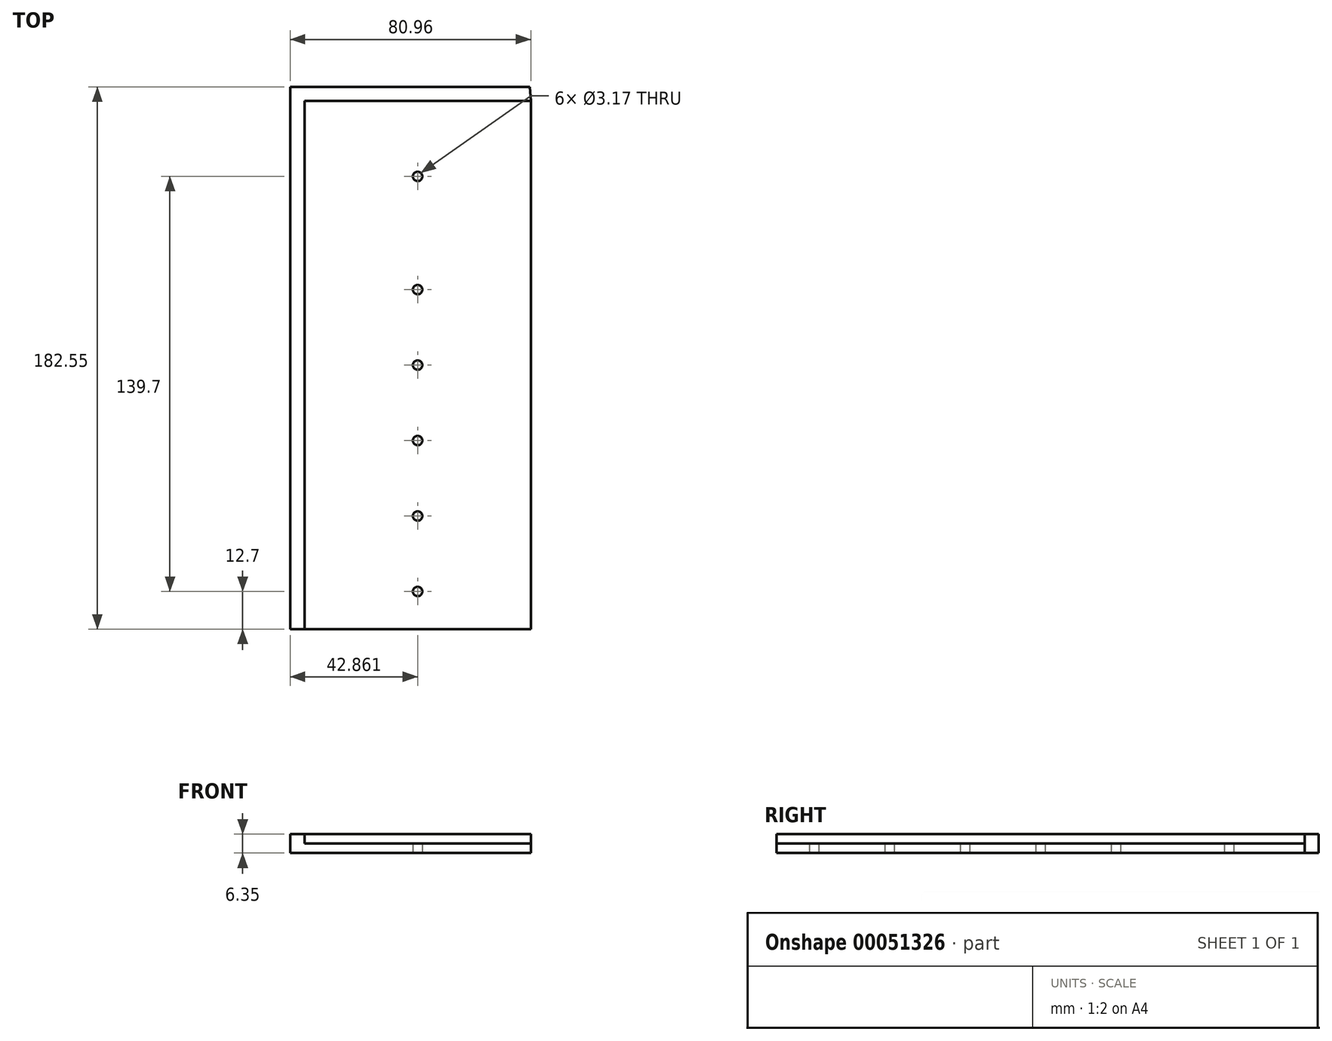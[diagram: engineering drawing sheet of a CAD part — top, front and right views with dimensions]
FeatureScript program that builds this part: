
annotation { "Feature Type Name" : "Feature", "Feature Type Description" : "" }
export const myFeature = defineFeature(function(context is Context, id is Id, definition is map)
    precondition{}
    {
        {
            var Q0;
            Q0=qCreatedBy(makeId("Top.planeOp"),FACE);
            var sketch = newSketch(context, id + "F0", { "sketchPlane" : qUnion([Q0])});
            skLineSegment(sketch, "E0.bottom", {"start": v(-43.27, -87.2) * mm, "end": v(32.93, -87.2) * mm});
            skLineSegment(sketch, "E0.top", {"start": v(-43.27, 90.6) * mm, "end": v(32.93, 90.6) * mm});
            skLineSegment(sketch, "E0.left", {"start": v(-43.27, -87.2) * mm, "end": v(-43.27, 90.6) * mm});
            skLineSegment(sketch, "E0.right", {"start": v(32.93, -87.2) * mm, "end": v(32.93, 90.6) * mm});
            skCircle(sketch, "E1", {"center": v(-5.17, 65.2) * mm, "radius": 1.59 * mm});
            skCircle(sketch, "E2", {"center": v(-5.17, 27.1) * mm, "radius": 1.59 * mm});
            skCircle(sketch, "E3", {"center": v(-5.17, 1.7) * mm, "radius": 1.59 * mm});
            skCircle(sketch, "E4", {"center": v(-5.17, -23.7) * mm, "radius": 1.59 * mm});
            skCircle(sketch, "E5", {"center": v(-5.17, -49.1) * mm, "radius": 1.59 * mm});
            skCircle(sketch, "E6", {"center": v(-5.17, -74.5) * mm, "radius": 1.59 * mm});
            skLineSegment(sketch, "E7", {"start": v(-43.27, -87.2) * mm, "end": v(-48.03, -87.2) * mm});
            skLineSegment(sketch, "E8", {"start": v(-48.03, -87.2) * mm, "end": v(-48.03, 95.34) * mm});
            skLineSegment(sketch, "E9", {"start": v(-48.03, 95.34) * mm, "end": v(32.58, 95.34) * mm});
            skLineSegment(sketch, "E10", {"start": v(32.58, 95.34) * mm, "end": v(32.93, 90.6) * mm});
            skSolve(sketch);
        }
        {
            var Q0;
            Q0=makeQuery(id+"F0.imprint","IMPRINT",FACE,{"disambiguationData":[TD([[makeQuery(id+"F0.imprint","IMPRINT",EDGE,{"derivedFrom":sQuery(id+"F0.wireOp",EDGE,"E0.top")}),1.0]])]});
            extrude(context, id + "F1", {"entities" : qUnion([Q0]), "depth" : 6.35 * mm});
        }
        {
            var Q0;
            Q0=qSketchRegion(id+"F0",true);
            extrude(context, id + "F2", {"entities" : qUnion([Q0]), "operationType" : NewBodyOperationType.ADD, "depth" : 3.17 * mm});
        }
    });
